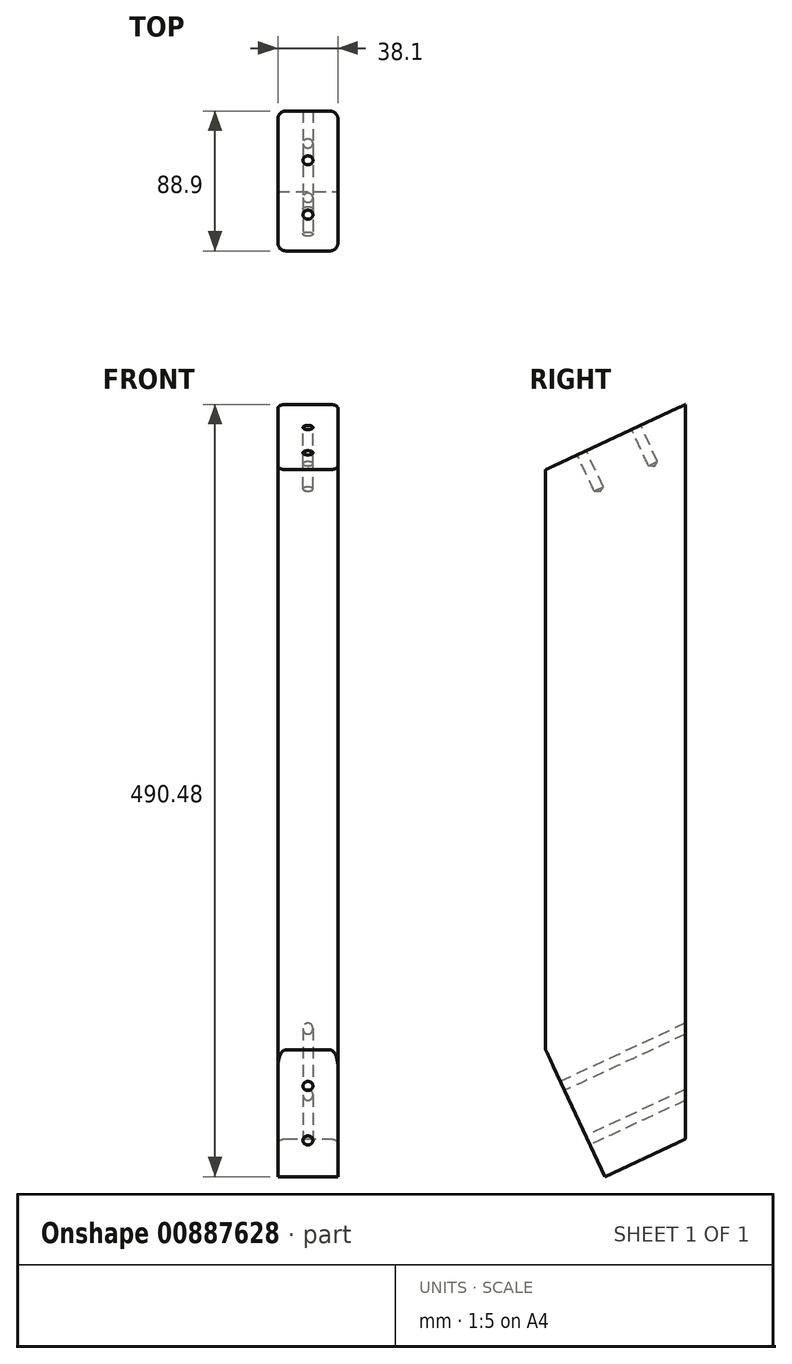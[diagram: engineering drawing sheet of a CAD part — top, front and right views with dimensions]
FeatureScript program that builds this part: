
annotation { "Feature Type Name" : "Feature", "Feature Type Description" : "" }
export const myFeature = defineFeature(function(context is Context, id is Id, definition is map)
    precondition{}
    {
        {
            var Q0;
            Q0=qCreatedBy(makeId("Top.planeOp"),FACE);
            var sketch = newSketch(context, id + "F0", { "sketchPlane" : qUnion([Q0])});
            skLineSegment(sketch, "E0.bottom", {"start": v(19.05, 44.45) * mm, "end": v(-19.05, 44.45) * mm});
            skLineSegment(sketch, "E0.top", {"start": v(19.05, -44.45) * mm, "end": v(-19.05, -44.45) * mm});
            skLineSegment(sketch, "E0.left", {"start": v(19.05, 44.45) * mm, "end": v(19.05, -44.45) * mm});
            skLineSegment(sketch, "E0.right", {"start": v(-19.05, 44.45) * mm, "end": v(-19.05, -44.45) * mm});
            skPoint(sketch, "E0.middle", {"position": v(0, 0) * mm});
            skSolve(sketch);
        }
        {
            var Q0;
            Q0=makeQuery(id+"F0.imprint","IMPRINT",FACE,{"disambiguationData":[TD([[makeQuery(id+"F0.imprint","IMPRINT",EDGE,{"derivedFrom":sQuery(id+"F0.wireOp",EDGE,"E0.bottom")}),1.0]])]});
            extrude(context, id + "F1", {"entities" : qUnion([Q0]), "endBound" : BoundingType.SYMMETRIC, "depth" : 508 * mm, "offsetDistance" : 25.4 * mm});
        }
        {
            var Q0;
            Q0=makeQuery(id+"F1.opExtrude","SWEPT_FACE",FACE,{"disambiguationData":[OSD([sQuery(id+"F0.wireOp",EDGE,"E0.left")])]});
            var sketch = newSketch(context, id + "F2", { "sketchPlane" : qUnion([Q0])});
            skLineSegment(sketch, "E1", {"start": v(-44.45, -254) * mm, "end": v(44.45, -212.55) * mm});
            skLineSegment(sketch, "E2", {"start": v(44.45, -212.55) * mm, "end": v(44.45, -254) * mm});
            skLineSegment(sketch, "E3", {"start": v(44.45, -254) * mm, "end": v(-44.45, -254) * mm});
            skLineSegment(sketch, "E4", {"start": v(-6.88, -236.48) * mm, "end": v(-44.45, -155.9) * mm});
            skLineSegment(sketch, "E5", {"start": v(-44.45, -155.9) * mm, "end": v(-44.45, -254) * mm});
            skLineSegment(sketch, "E6", {"start": v(44.45, 254) * mm, "end": v(-44.45, 212.55) * mm});
            skLineSegment(sketch, "E7", {"start": v(-44.45, 212.55) * mm, "end": v(-44.45, 254) * mm});
            skLineSegment(sketch, "E8", {"start": v(-44.45, 254) * mm, "end": v(44.45, 254) * mm});
            skSolve(sketch);
        }
        {
            var Q0;
            Q0=makeQuery(id+"F2.imprint","IMPRINT",FACE,{"disambiguationData":[TD([[makeQuery(id+"F2.imprint","IMPRINT",EDGE,{"derivedFrom":sQuery(id+"F2.wireOp",EDGE,"E6")}),-1.0]])]});
            var Q1;
            {var subQ3=sQuery(id+"F2.wireOp",EDGE,"E2");Q1=makeQuery(id+"F2.imprint","IMPRINT",FACE,{"disambiguationData":[TD([[makeQuery(id+"F2.imprint","IMPRINT",EDGE,{"derivedFrom":subQ3}),-1.0]])]});}
            var Q2;
            {var subQ2=sQuery(id+"F2.wireOp",EDGE,"E4");Q2=makeQuery(id+"F2.imprint","IMPRINT",FACE,{"disambiguationData":[TD([[makeQuery(id+"F2.imprint","IMPRINT",EDGE,{"derivedFrom":subQ2}),1.0]])]});}
            extrude(context, id + "F3", {"entities" : qUnion([Q0, Q1, Q2]), "operationType" : NewBodyOperationType.REMOVE, "endBound" : BoundingType.THROUGH_ALL, "oppositeDirection" : true, "depth" : 25.4 * mm, "offsetDistance" : 25.4 * mm});
        }
        {
            var Q0;
            Q0=makeQuery(id+"F3.boolean.opBoolean","COPY",FACE,{"derivedFrom":makeQuery(id+"F3.opExtrude","SWEPT_FACE",FACE,{"disambiguationData":[OSD([sQuery(id+"F2.wireOp",EDGE,"E4")])]})});
            var sketch = newSketch(context, id + "F4", { "sketchPlane" : qUnion([Q0])});
            skPoint(sketch, "E9", {"position": v(0, -147.92) * mm});
            skPoint(sketch, "E10", {"position": v(0, -186.02) * mm});
            skSolve(sketch);
        }
        {
            var Q0;
            Q0=sQuery(id+"F4.wireOp",VERTEX,"E9");
            var Q1;
            Q1=sQuery(id+"F4.wireOp",VERTEX,"E10");
            var Q2;
            Q2=makeQuery(id+"F1.opExtrude","SWEPT_BODY",BODY,{"disambiguationData":[OSD([sQuery(id+"F0.wireOp",EDGE,"E0.bottom"),sQuery(id+"F0.wireOp",EDGE,"E0.top"),sQuery(id+"F0.wireOp",EDGE,"E0.left"),sQuery(id+"F0.wireOp",EDGE,"E0.right")])]});
            hole(context, id + "F5", {"style" : HoleStyle.SIMPLE, "endStyle" : HoleEndStyle.THROUGH, "holeDiameter" : 6.35 * mm, "majorDiameter" : 6.35 * mm, "isTappedThrough" : true, "tappedDepth" : 12.7 * mm, "tapClearance" : 3, "locations" : qUnion([Q0, Q1]), "scope" : qUnion([Q2])});
        }
        {
            var Q0;
            Q0=makeQuery(id+"F1.opExtrude","SWEPT_EDGE",EDGE,{"disambiguationData":[OSD([sQuery(id+"F0.wireOp",EDGE,"E0.top"),sQuery(id+"F0.wireOp",EDGE,"E0.left")])]});
            var Q1;
            Q1=makeQuery(id+"F1.opExtrude","SWEPT_EDGE",EDGE,{"disambiguationData":[OSD([sQuery(id+"F0.wireOp",EDGE,"E0.top"),sQuery(id+"F0.wireOp",EDGE,"E0.right")])]});
            var Q2;
            Q2=makeQuery(id+"F1.opExtrude","SWEPT_EDGE",EDGE,{"disambiguationData":[OSD([sQuery(id+"F0.wireOp",EDGE,"E0.bottom"),sQuery(id+"F0.wireOp",EDGE,"E0.left")])]});
            var Q3;
            Q3=makeQuery(id+"F1.opExtrude","SWEPT_EDGE",EDGE,{"disambiguationData":[OSD([sQuery(id+"F0.wireOp",EDGE,"E0.bottom"),sQuery(id+"F0.wireOp",EDGE,"E0.right")])]});
            fillet(context, id + "F6", {"entities" : qUnion([Q0, Q1, Q2, Q3]), "radius" : 5.08 * mm, "tangentPropagation" : true, "allowEdgeOverflow" : false});
        }
        {
            var Q0;
            Q0=makeQuery(id+"F3.boolean.opBoolean","COPY",FACE,{"derivedFrom":makeQuery(id+"F3.opExtrude","SWEPT_FACE",FACE,{"disambiguationData":[OSD([sQuery(id+"F2.wireOp",EDGE,"E6")])]})});
            var sketch = newSketch(context, id + "F7", { "sketchPlane" : qUnion([Q0])});
            skPoint(sketch, "E11", {"position": v(0, 113.04) * mm});
            skPoint(sketch, "E12", {"position": v(0, 74.94) * mm});
            skSolve(sketch);
        }
        {
            var Q0;
            Q0=sQuery(id+"F7.wireOp",VERTEX,"E11");
            var Q1;
            Q1=sQuery(id+"F7.wireOp",VERTEX,"E12");
            var Q2;
            Q2=makeQuery(id+"F1.opExtrude","SWEPT_BODY",BODY,{"disambiguationData":[OSD([sQuery(id+"F0.wireOp",EDGE,"E0.bottom"),sQuery(id+"F0.wireOp",EDGE,"E0.top"),sQuery(id+"F0.wireOp",EDGE,"E0.left"),sQuery(id+"F0.wireOp",EDGE,"E0.right")])]});
            hole(context, id + "F8", {"style" : HoleStyle.SIMPLE, "endStyle" : HoleEndStyle.BLIND, "holeDiameter" : 6.35 * mm, "majorDiameter" : 6.35 * mm, "holeDepth" : 25.4 * mm, "isTappedThrough" : true, "tappedDepth" : 12.7 * mm, "tapClearance" : 3, "locations" : qUnion([Q0, Q1]), "scope" : qUnion([Q2])});
        }
    });
